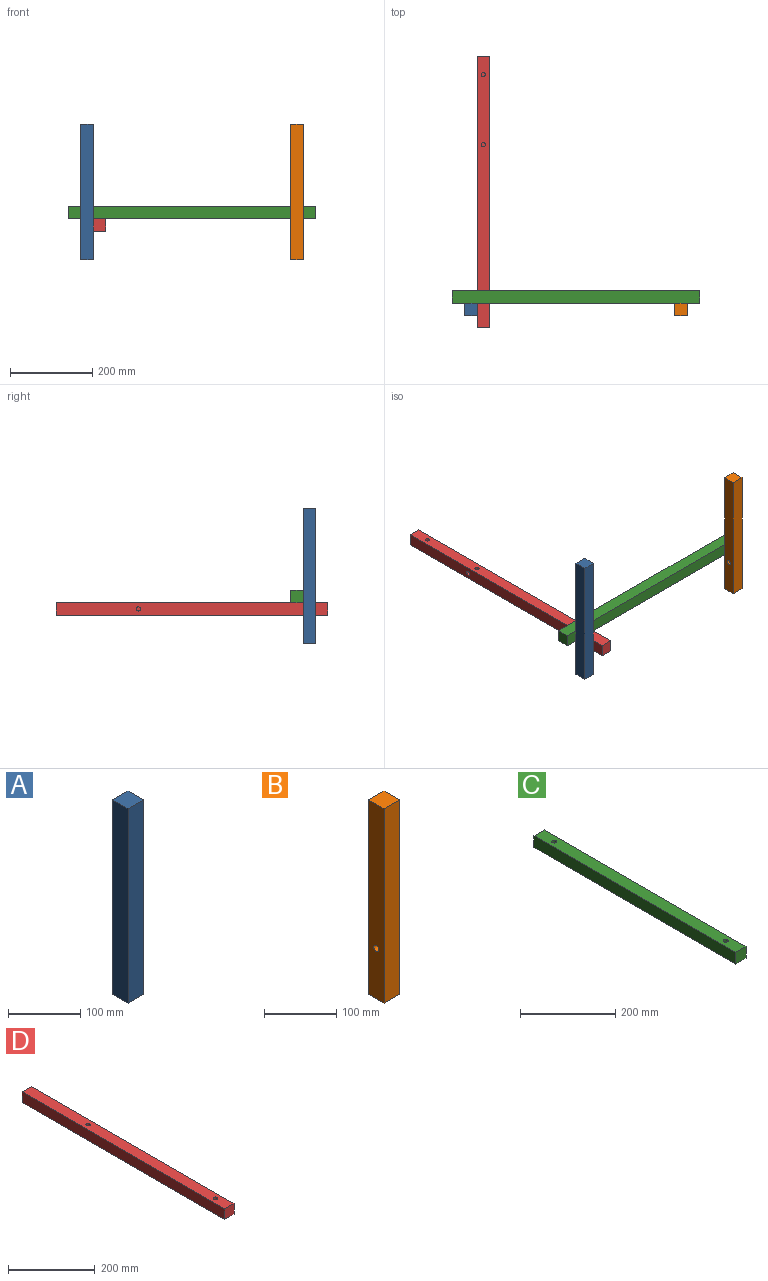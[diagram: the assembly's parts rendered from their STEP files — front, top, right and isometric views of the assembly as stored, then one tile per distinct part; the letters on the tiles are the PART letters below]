
ASSEMBLY  parts=4 mates=8
PART A: 12 faces, bbox 30x30x330 mm
  f0: plane 330x30mm, normal (1,0,0), area 9821.5mm2, adj f1,f3,f4,f5,f10
  f1: plane 330x30mm, normal (0,1,0), area 9742.9mm2, adj f0,f2,f4,f5,f6,f8
  f2: plane 330x30mm, normal (-1,0,0), area 9900mm2, adj f1,f3,f4,f5
  f3: plane 330x30mm, normal (0,-1,0), area 9900mm2, adj f0,f2,f4,f5
  f4: plane 30x30mm, normal (0,0,1), area 900mm2, adj f0,f1,f2,f3
  f5: plane 30x30mm, normal (0,0,-1), area 900mm2, adj f0,f1,f2,f3
  f6: cylinder r=5mm len=15mm, axis (0,1,0), area 471.2mm2, adj f1,f7
  f7: plane 10x10mm, normal (0,1,0), area 78.5mm2, adj f6
  f8: cylinder r=5mm len=15mm, axis (0,1,0), area 471.2mm2, adj f1,f9
  f9: plane 10x10mm, normal (0,1,0), area 78.5mm2, adj f8
  f10: cylinder r=5mm len=15mm, axis (1,0,0), area 471.2mm2, adj f0,f11
  f11: plane 10x10mm, normal (1,0,0), area 78.5mm2, adj f10
PART B: 12 faces, bbox 30x30x330 mm
  f0: plane 330x30mm, normal (1,0,0), area 9900mm2, adj f1,f3,f4,f5
  f1: plane 330x30mm, normal (0,1,0), area 9742.9mm2, adj f0,f2,f4,f5,f6,f8
  f2: plane 330x30mm, normal (-1,0,0), area 9821.5mm2, adj f1,f3,f4,f5,f10
  f3: plane 330x30mm, normal (0,-1,0), area 9900mm2, adj f0,f2,f4,f5
  f4: plane 30x30mm, normal (0,0,1), area 900mm2, adj f0,f1,f2,f3
  f5: plane 30x30mm, normal (0,0,-1), area 900mm2, adj f0,f1,f2,f3
  f6: cylinder r=5mm len=15mm, axis (0,1,0), area 471.2mm2, adj f1,f7
  f7: plane 10x10mm, normal (0,1,0), area 78.5mm2, adj f6
  f8: cylinder r=5mm len=15mm, axis (0,1,0), area 471.2mm2, adj f1,f9
  f9: plane 10x10mm, normal (0,1,0), area 78.5mm2, adj f8
  f10: cylinder r=5mm len=25mm, axis (-1,0,0), area 785.4mm2, adj f2,f11
  f11: plane 10x10mm, normal (-1,0,0), area 78.5mm2, adj f10
PART C: 14 faces, bbox 30x600x30 mm
  f0: plane 600x30mm, normal (1,0,0), area 17842.9mm2, adj f1,f3,f4,f5,f10,f12
  f1: plane 600x30mm, normal (0,0,1), area 17842.9mm2, adj f0,f2,f4,f5,f6,f8
  f2: plane 600x30mm, normal (-1,0,0), area 18000mm2, adj f1,f3,f4,f5
  f3: plane 600x30mm, normal (0,0,-1), area 18000mm2, adj f0,f2,f4,f5
  f4: plane 30x30mm, normal (0,-1,0), area 900mm2, adj f0,f1,f2,f3
  f5: plane 30x30mm, normal (0,1,0), area 900mm2, adj f0,f1,f2,f3
  f6: cylinder r=5mm len=15mm, axis (0,0,1), area 471.2mm2, adj f1,f7
  f7: plane 10x10mm, normal (0,0,1), area 78.5mm2, adj f6
  f8: cylinder r=5mm len=15mm, axis (0,0,1), area 471.2mm2, adj f1,f9
  f9: plane 10x10mm, normal (0,0,1), area 78.5mm2, adj f8
  f10: cylinder r=5mm len=15mm, axis (1,0,0), area 471.2mm2, adj f0,f11
  f11: plane 10x10mm, normal (1,0,0), area 78.5mm2, adj f10
  f12: cylinder r=5mm len=15mm, axis (1,0,0), area 471.2mm2, adj f0,f13
  f13: plane 10x10mm, normal (1,0,0), area 78.5mm2, adj f12
PART D: 16 faces, bbox 30x660x30 mm
  f0: plane 660x30mm, normal (1,0,0), area 19564.4mm2, adj f1,f3,f4,f5,f6,f8,f10
  f1: plane 660x30mm, normal (0,0,1), area 19642.9mm2, adj f0,f2,f4,f5,f12,f14
  f2: plane 660x30mm, normal (-1,0,0), area 19800mm2, adj f1,f3,f4,f5
  f3: plane 660x30mm, normal (0,0,-1), area 19800mm2, adj f0,f2,f4,f5
  f4: plane 30x30mm, normal (0,-1,0), area 900mm2, adj f0,f1,f2,f3
  f5: plane 30x30mm, normal (0,1,0), area 900mm2, adj f0,f1,f2,f3
  f6: cylinder r=5mm len=15mm, axis (1,0,0), area 471.2mm2, adj f0,f7
  f7: plane 10x10mm, normal (1,0,0), area 78.5mm2, adj f6
  f8: cylinder r=5mm len=15mm, axis (1,0,0), area 471.2mm2, adj f0,f9
  f9: plane 10x10mm, normal (1,0,0), area 78.5mm2, adj f8
  f10: cylinder r=5mm len=15mm, axis (1,0,0), area 471.2mm2, adj f0,f11
  f11: plane 10x10mm, normal (1,0,0), area 78.5mm2, adj f10
  f12: cylinder r=5mm len=15mm, axis (0,0,1), area 471.2mm2, adj f1,f13
  f13: plane 10x10mm, normal (0,0,1), area 78.5mm2, adj f12
  f14: cylinder r=5mm len=15mm, axis (0,0,1), area 471.2mm2, adj f1,f15
  f15: plane 10x10mm, normal (0,0,1), area 78.5mm2, adj f14
PLACE A t=(-510,0,0)mm
PLACE B at identity fixed
PLACE C rot(axis=(0.58,0.58,-0.58),120deg) t=(45,30,115)mm
PLACE D rot(axis=(0,-1,0),90deg) t=(-480,615,85)mm
MATE parallel B.f4 <-> C.f0  axis (0,0,1) through (0,0,330)mm
MATE parallel A.f4 <-> C.f2  axis (0,0,1) through (-510,0,330)mm
MATE slider C.f6 <-> B.f8  axis (0,-1,0) through (0,22.5,115)mm
MATE planar D.f0 <-> C.f0  axis (0,0,1) through (-480,284.42,100)mm
MATE slider D.f10 <-> C.f10  axis (0,0,1) through (-480,30,92.5)mm
MATE planar C.f1 <-> A.f1  axis (0,-1,0) through (-255,15,115)mm
MATE planar B.f1 <-> C.f6  axis (0,1,0) through (0,15,164.44)mm
MATE slider A.f8 <-> C.f8  axis (0,1,0) through (-510,7.5,115)mm
